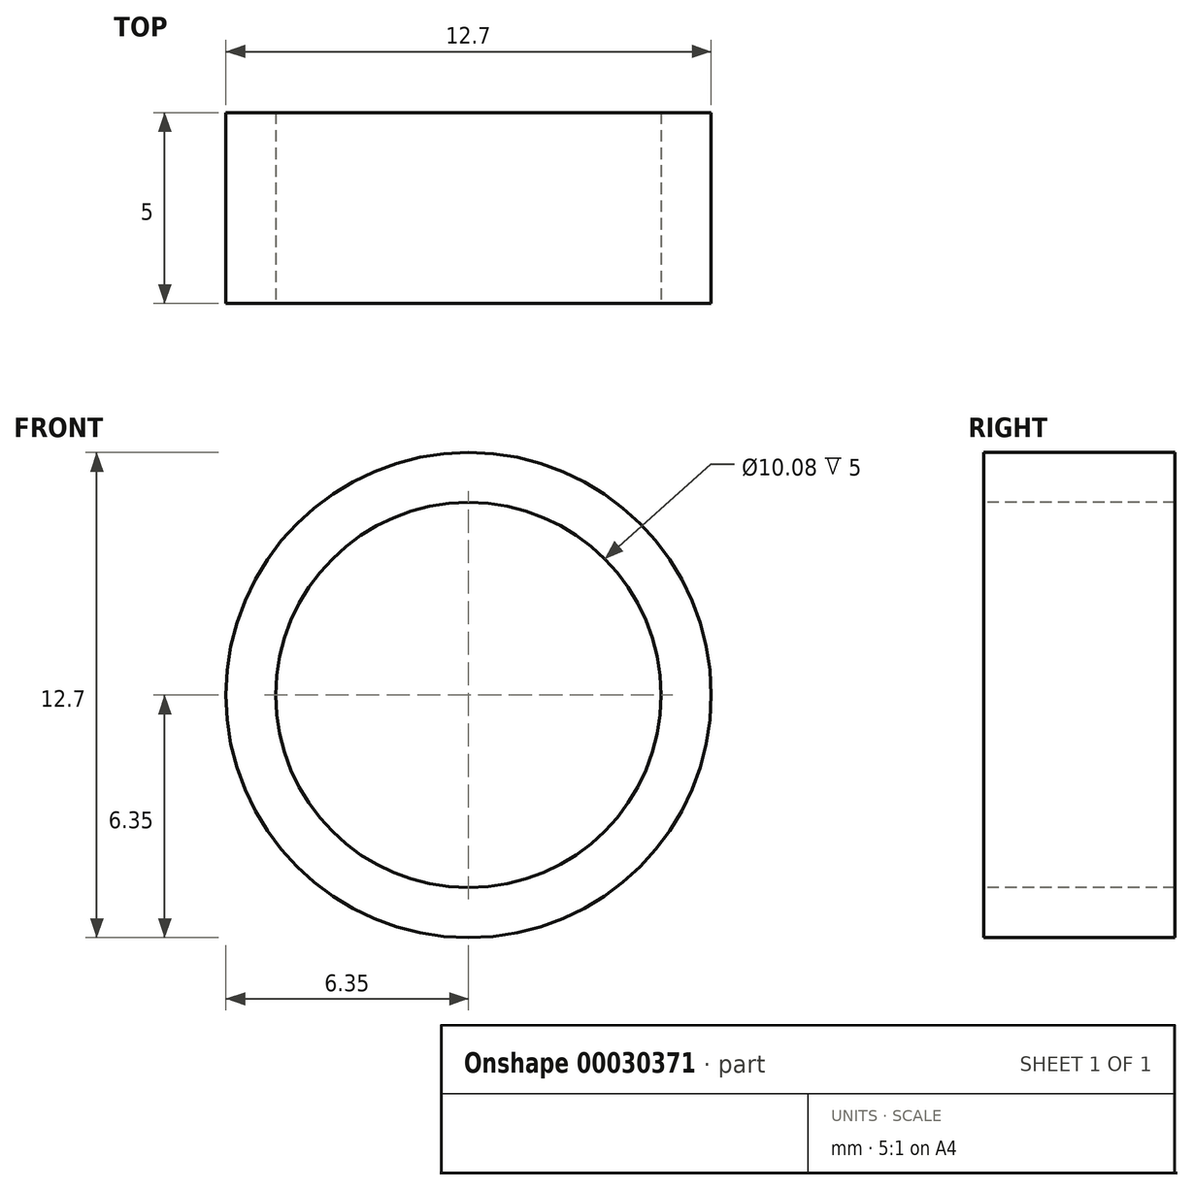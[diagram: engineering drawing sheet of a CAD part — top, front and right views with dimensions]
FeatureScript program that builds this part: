
annotation { "Feature Type Name" : "Feature", "Feature Type Description" : "" }
export const myFeature = defineFeature(function(context is Context, id is Id, definition is map)
    precondition{}
    {
        {
            var Q0;
            Q0=qCreatedBy(makeId("Front.planeOp"),FACE);
            var sketch = newSketch(context, id + "F0", { "sketchPlane" : qUnion([Q0])});
            skCircle(sketch, "E0", {"center": v(0, 0) * mm, "radius": 6.35 * mm});
            skSolve(sketch);
        }
        {
            var Q0;
            Q0 = qSketchRegion(id + "F0", true);
            extrude(context, id + "F1", {"entities" : qUnion([Q0]), "depth" : 5 * mm});
        }
        {
            var Q0;
            Q0=makeQuery(id+"F1.opExtrude","CAP_FACE",FACE,{"disambiguationData":[OSD([sQuery(id+"F0.wireOp",EDGE,"E0")])],"isStart":false});
            var sketch = newSketch(context, id + "F2", { "sketchPlane" : qUnion([Q0])});
            skPoint(sketch, "E1", {"position": v(0, 0) * mm});
            skSolve(sketch);
        }
        {
            var Q0;
            Q0=sQuery(id+"F2.wireOp",VERTEX,"E1");
            var Q1;
            Q1=makeQuery(id+"F1.opExtrude","SWEPT_BODY",BODY,{"disambiguationData":[OSD([sQuery(id+"F0.wireOp",EDGE,"E0")])]});
            hole(context, id + "F3", {"style" : HoleStyle.SIMPLE, "endStyle" : HoleEndStyle.THROUGH, "standardTappedOrClearance" : lookupTablePath({ "standard" : "ANSI", "size" : "X (0.4)", "type" : "Drilled" }), "standardBlindInLast" : lookupTablePath({ "standard" : "ANSI", "size" : "X", "type" : "Drilled" }), "holeDiameter" : 10.08 * mm, "locations" : qUnion([Q0]), "scope" : qUnion([Q1]), "isTappedThrough" : true});
        }
    });
